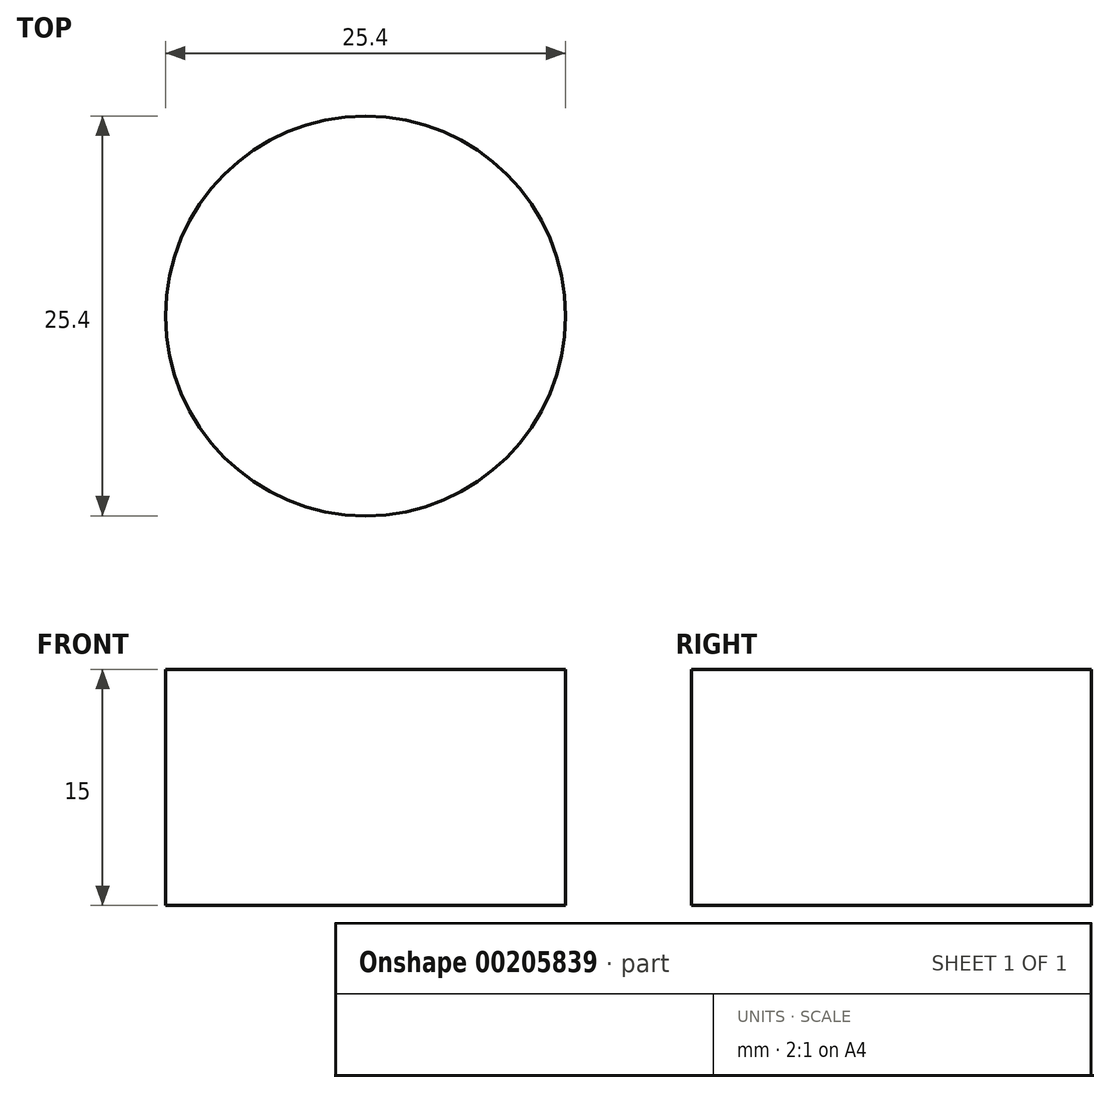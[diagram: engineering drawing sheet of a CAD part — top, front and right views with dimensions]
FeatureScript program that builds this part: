
annotation { "Feature Type Name" : "Feature", "Feature Type Description" : "" }
export const myFeature = defineFeature(function(context is Context, id is Id, definition is map)
    precondition{}
    {
        {
            assignVariable(context, id + "F0", {"name" : "BarPosPerc", "anyValue" : 0.3});
        }
        {
            assignVariable(context, id + "F1", {"name" : "BarLong", "anyValue" : 15});
        }
        {
            var Q0;
            Q0=qCreatedBy(makeId("Top.planeOp"),FACE);
            var sketch = newSketch(context, id + "F2", { "sketchPlane" : qUnion([Q0])});
            skCircle(sketch, "E0", {"center": v(0, 0) * mm, "radius": 12.7 * mm});
            skSolve(sketch);
        }
        {
            var Q0;
            Q0=makeQuery(id+"F2.imprint","IMPRINT",FACE,{"disambiguationData":[TD([[makeQuery(id+"F2.imprint","IMPRINT",EDGE,{"derivedFrom":sQuery(id+"F2.wireOp",EDGE,"E0")}),1.0]])]});
            var Q1;
            Q1=sQuery(id+"F2.wireOp",EDGE,"E0");
            extrude(context, id + "F3", {"entities" : qUnion([Q0]), "surfaceEntities" : qUnion([Q1]), "depth" : ((1 - getVariable(context, 'BarPosPerc')) * getVariable(context, 'BarLong')) * mm, "hasSecondDirection" : true, "secondDirectionOppositeDirection" : true, "secondDirectionDepth" : (getVariable(context, 'BarPosPerc') * getVariable(context, 'BarLong')) * mm});
        }
    });
